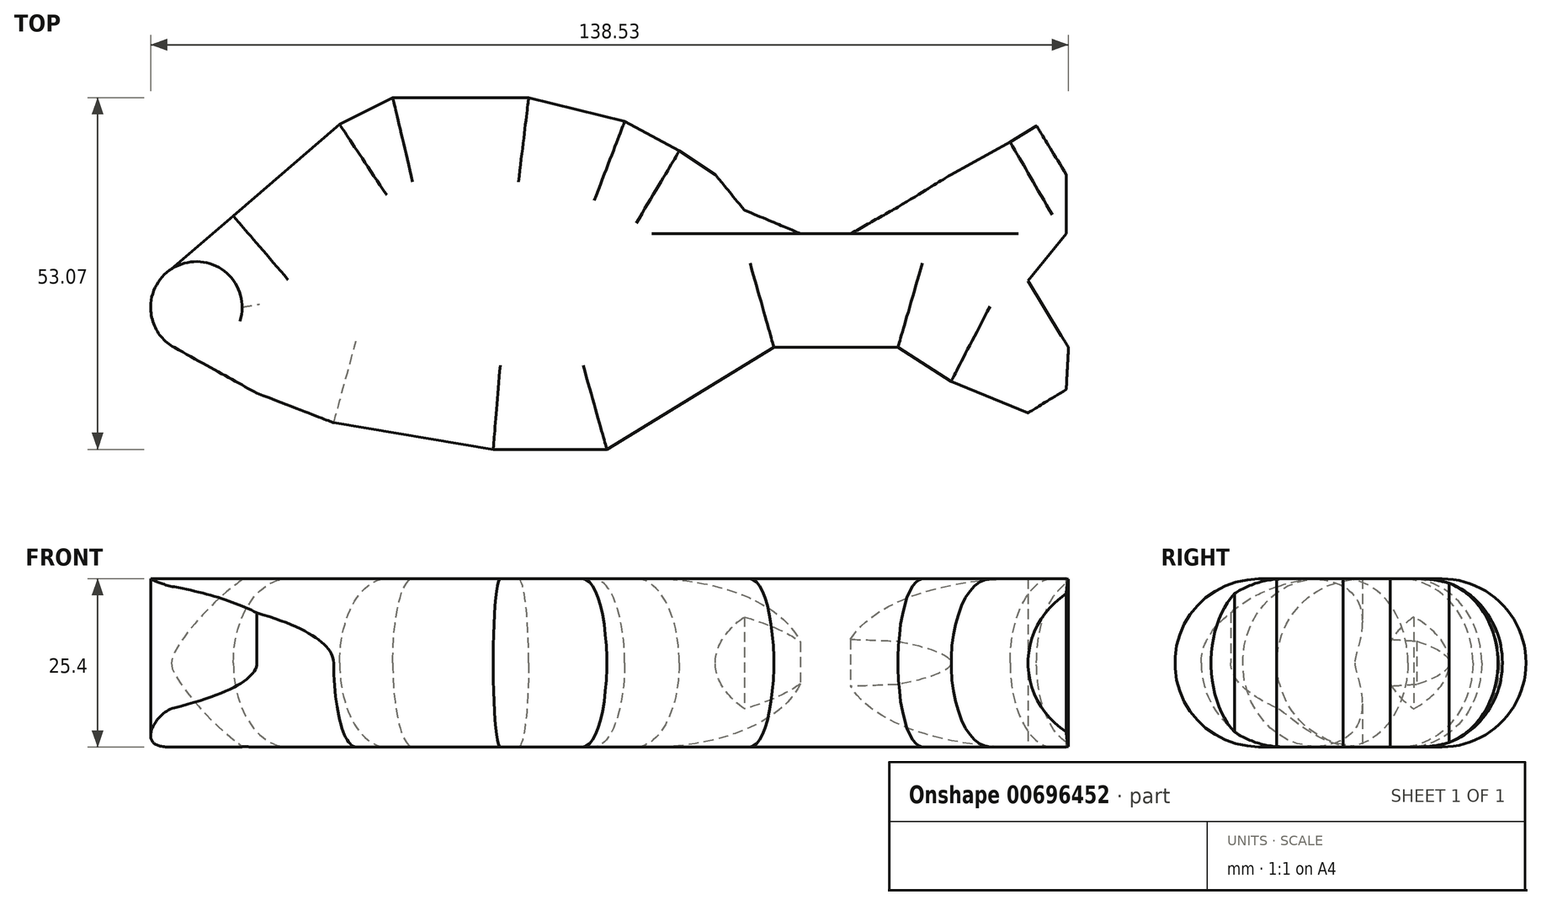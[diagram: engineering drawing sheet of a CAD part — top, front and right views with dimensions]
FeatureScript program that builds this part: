
annotation { "Feature Type Name" : "Feature", "Feature Type Description" : "" }
export const myFeature = defineFeature(function(context is Context, id is Id, definition is map)
    precondition{}
    {
        {
            var Q0;
            Q0=qCreatedBy(makeId("Top.planeOp"),FACE);
            var sketch = newSketch(context, id + "F0", { "sketchPlane" : qUnion([Q0])});
            skLineSegment(sketch, "E0", {"start": v(-59.07, 19.84) * mm, "end": v(-43.02, 33.66) * mm});
            skLineSegment(sketch, "E1", {"start": v(-43.02, 33.66) * mm, "end": v(-35, 37.67) * mm});
            skLineSegment(sketch, "E2", {"start": v(-35, 37.67) * mm, "end": v(-30.98, 37.67) * mm});
            skLineSegment(sketch, "E3", {"start": v(-30.98, 37.67) * mm, "end": v(-14.49, 37.67) * mm});
            skLineSegment(sketch, "E4", {"start": v(-14.49, 37.67) * mm, "end": v(0, 34.1) * mm});
            skLineSegment(sketch, "E5", {"start": v(0, 34.1) * mm, "end": v(8.25, 29.65) * mm});
            skLineSegment(sketch, "E6", {"start": v(8.25, 29.65) * mm, "end": v(13.68, 26.08) * mm});
            skLineSegment(sketch, "E7", {"start": v(13.68, 26.08) * mm, "end": v(18.06, 20.73) * mm});
            skLineSegment(sketch, "E8", {"start": v(18.06, 20.73) * mm, "end": v(26.53, 17.16) * mm});
            skLineSegment(sketch, "E9", {"start": v(26.53, 17.16) * mm, "end": v(34.1, 17.16) * mm});
            skLineSegment(sketch, "E10", {"start": v(34.1, 17.16) * mm, "end": v(41.24, 21.18) * mm});
            skLineSegment(sketch, "E11", {"start": v(41.24, 21.18) * mm, "end": v(49.26, 26.08) * mm});
            skLineSegment(sketch, "E12", {"start": v(49.26, 26.08) * mm, "end": v(58.18, 30.98) * mm});
            skLineSegment(sketch, "E13", {"start": v(58.18, 30.98) * mm, "end": v(62.17, 33.42) * mm});
            skLineSegment(sketch, "E14", {"start": v(62.17, 33.42) * mm, "end": v(66.65, 26.08) * mm});
            skLineSegment(sketch, "E15", {"start": v(66.65, 26.08) * mm, "end": v(66.65, 17.16) * mm});
            skLineSegment(sketch, "E16", {"start": v(66.65, 17.16) * mm, "end": v(60.85, 10.03) * mm});
            skLineSegment(sketch, "E17", {"start": v(60.85, 10.03) * mm, "end": v(66.98, 0) * mm});
            skLineSegment(sketch, "E18", {"start": v(66.98, 0) * mm, "end": v(66.65, -6.35) * mm});
            skLineSegment(sketch, "E19", {"start": v(66.65, -6.35) * mm, "end": v(60.85, -9.9) * mm});
            skLineSegment(sketch, "E20", {"start": v(60.85, -9.9) * mm, "end": v(49.26, -5.13) * mm});
            skLineSegment(sketch, "E21", {"start": v(49.26, -5.13) * mm, "end": v(41.24, 0) * mm});
            skLineSegment(sketch, "E22", {"start": v(41.24, 0) * mm, "end": v(32.32, 0) * mm});
            skLineSegment(sketch, "E23", {"start": v(32.32, 0) * mm, "end": v(22.51, 0) * mm});
            skLineSegment(sketch, "E24", {"start": v(22.51, 0) * mm, "end": v(17.7, -2.94) * mm});
            skLineSegment(sketch, "E25", {"start": v(17.7, -2.94) * mm, "end": v(5.25, -10.55) * mm});
            skLineSegment(sketch, "E26", {"start": v(5.25, -10.55) * mm, "end": v(-2.69, -15.4) * mm});
            skLineSegment(sketch, "E27", {"start": v(-2.69, -15.4) * mm, "end": v(-19.84, -15.4) * mm});
            skLineSegment(sketch, "E28", {"start": v(-19.84, -15.4) * mm, "end": v(-43.91, -11.37) * mm});
            skLineSegment(sketch, "E29", {"start": v(-43.91, -11.37) * mm, "end": v(-55.5, -6.91) * mm});
            skLineSegment(sketch, "E30", {"start": v(-59.07, 19.84) * mm, "end": v(-68.43, 11.81) * mm});
            skLineSegment(sketch, "E31", {"start": v(-55.5, -6.91) * mm, "end": v(-67.99, 0) * mm});
            skArc(sketch, "E32", {"start": v(-68.43, 11.81) * mm, "mid": v(-71.54, 5.78) * mm, "end": v(-67.99, 0) * mm});
            skSolve(sketch);
        }
        {
            var Q0;
            Q0 = qSketchRegion(id + "F0", true);
            extrude(context, id + "F1", {"entities" : qUnion([Q0]), "depth" : 25.4 * mm, "offsetDistance" : 25.4 * mm});
        }
        {
            var Q0;
            Q0=makeQuery(id+"F1.opExtrude","CAP_EDGE",EDGE,{"disambiguationData":[OSD([sQuery(id+"F0.wireOp",EDGE,"E0")])],"isStart":false});
            var Q1;
            Q1=makeQuery(id+"F1.opExtrude","CAP_EDGE",EDGE,{"disambiguationData":[OSD([sQuery(id+"F0.wireOp",EDGE,"E1")])],"isStart":false});
            var Q2;
            Q2=makeQuery(id+"F1.opExtrude","CAP_EDGE",EDGE,{"disambiguationData":[OSD([sQuery(id+"F0.wireOp",EDGE,"E2"),sQuery(id+"F0.wireOp",EDGE,"E3")])],"isStart":false});
            var Q3;
            Q3=makeQuery(id+"F1.opExtrude","CAP_EDGE",EDGE,{"disambiguationData":[OSD([sQuery(id+"F0.wireOp",EDGE,"E4")])],"isStart":false});
            var Q4;
            Q4=makeQuery(id+"F1.opExtrude","CAP_EDGE",EDGE,{"disambiguationData":[OSD([sQuery(id+"F0.wireOp",EDGE,"E5")])],"isStart":false});
            var Q5;
            Q5=makeQuery(id+"F1.opExtrude","CAP_EDGE",EDGE,{"disambiguationData":[OSD([sQuery(id+"F0.wireOp",EDGE,"E6")])],"isStart":false});
            fillet(context, id + "F2", {"entities" : qUnion([Q0, Q1, Q2, Q3, Q4, Q5]), "radius" : 12.7 * mm, "tangentPropagation" : true, "allowEdgeOverflow" : false});
        }
        {
            var Q0;
            Q0=makeQuery(id+"F1.opExtrude","CAP_EDGE",EDGE,{"disambiguationData":[OSD([sQuery(id+"F0.wireOp",EDGE,"E2"),sQuery(id+"F0.wireOp",EDGE,"E3")])],"isStart":true});
            var Q1;
            Q1=makeQuery(id+"F1.opExtrude","CAP_EDGE",EDGE,{"disambiguationData":[OSD([sQuery(id+"F0.wireOp",EDGE,"E4")])],"isStart":true});
            var Q2;
            Q2=makeQuery(id+"F1.opExtrude","CAP_EDGE",EDGE,{"disambiguationData":[OSD([sQuery(id+"F0.wireOp",EDGE,"E5")])],"isStart":true});
            var Q3;
            Q3=makeQuery(id+"F1.opExtrude","CAP_EDGE",EDGE,{"disambiguationData":[OSD([sQuery(id+"F0.wireOp",EDGE,"E0")])],"isStart":true});
            var Q4;
            Q4=makeQuery(id+"F1.opExtrude","CAP_EDGE",EDGE,{"disambiguationData":[OSD([sQuery(id+"F0.wireOp",EDGE,"E1")])],"isStart":true});
            var Q5;
            Q5=makeQuery(id+"F1.opExtrude","CAP_EDGE",EDGE,{"disambiguationData":[OSD([sQuery(id+"F0.wireOp",EDGE,"E6")])],"isStart":true});
            var Q6;
            Q6=makeQuery(id+"F1.opExtrude","CAP_EDGE",EDGE,{"disambiguationData":[OSD([sQuery(id+"F0.wireOp",EDGE,"E28")])],"isStart":true});
            var Q7;
            Q7=makeQuery(id+"F1.opExtrude","CAP_EDGE",EDGE,{"disambiguationData":[OSD([sQuery(id+"F0.wireOp",EDGE,"E29")])],"isStart":true});
            var Q8;
            Q8=makeQuery(id+"F1.opExtrude","CAP_EDGE",EDGE,{"disambiguationData":[OSD([sQuery(id+"F0.wireOp",EDGE,"E27")])],"isStart":true});
            var Q9;
            Q9=makeQuery(id+"F1.opExtrude","CAP_EDGE",EDGE,{"disambiguationData":[OSD([sQuery(id+"F0.wireOp",EDGE,"E24"),sQuery(id+"F0.wireOp",EDGE,"E25"),sQuery(id+"F0.wireOp",EDGE,"E26")])],"isStart":true});
            var Q10;
            Q10=makeQuery(id+"F1.opExtrude","CAP_EDGE",EDGE,{"disambiguationData":[OSD([sQuery(id+"F0.wireOp",EDGE,"E22"),sQuery(id+"F0.wireOp",EDGE,"E23")])],"isStart":true});
            var Q11;
            Q11=makeQuery(id+"F1.opExtrude","CAP_EDGE",EDGE,{"disambiguationData":[OSD([sQuery(id+"F0.wireOp",EDGE,"E21")])],"isStart":true});
            var Q12;
            Q12=makeQuery(id+"F1.opExtrude","CAP_EDGE",EDGE,{"disambiguationData":[OSD([sQuery(id+"F0.wireOp",EDGE,"E20")])],"isStart":true});
            var Q13;
            Q13=makeQuery(id+"F1.opExtrude","CAP_EDGE",EDGE,{"disambiguationData":[OSD([sQuery(id+"F0.wireOp",EDGE,"E12")])],"isStart":true});
            var Q14;
            Q14=makeQuery(id+"F1.opExtrude","CAP_EDGE",EDGE,{"disambiguationData":[OSD([sQuery(id+"F0.wireOp",EDGE,"E20")])],"isStart":false});
            var Q15;
            Q15=makeQuery(id+"F1.opExtrude","CAP_EDGE",EDGE,{"disambiguationData":[OSD([sQuery(id+"F0.wireOp",EDGE,"E21")])],"isStart":false});
            var Q16;
            Q16=makeQuery(id+"F1.opExtrude","CAP_EDGE",EDGE,{"disambiguationData":[OSD([sQuery(id+"F0.wireOp",EDGE,"E22"),sQuery(id+"F0.wireOp",EDGE,"E23")])],"isStart":false});
            var Q17;
            Q17=makeQuery(id+"F1.opExtrude","CAP_EDGE",EDGE,{"disambiguationData":[OSD([sQuery(id+"F0.wireOp",EDGE,"E24"),sQuery(id+"F0.wireOp",EDGE,"E25"),sQuery(id+"F0.wireOp",EDGE,"E26")])],"isStart":false});
            var Q18;
            Q18=makeQuery(id+"F1.opExtrude","CAP_EDGE",EDGE,{"disambiguationData":[OSD([sQuery(id+"F0.wireOp",EDGE,"E28")])],"isStart":false});
            var Q19;
            Q19=makeQuery(id+"F1.opExtrude","CAP_EDGE",EDGE,{"disambiguationData":[OSD([sQuery(id+"F0.wireOp",EDGE,"E27")])],"isStart":false});
            fillet(context, id + "F3", {"entities" : qUnion([Q0, Q1, Q2, Q3, Q4, Q5, Q6, Q7, Q8, Q9, Q10, Q11, Q12, Q13, Q14, Q15, Q16, Q17, Q18, Q19]), "radius" : 12.7 * mm, "tangentPropagation" : true, "allowEdgeOverflow" : false});
        }
        {
            var Q0;
            Q0=makeQuery(id+"F1.opExtrude","CAP_EDGE",EDGE,{"disambiguationData":[OSD([sQuery(id+"F0.wireOp",EDGE,"E28")])],"isStart":false});
            var Q1;
            Q1=makeQuery(id+"F1.opExtrude","CAP_EDGE",EDGE,{"disambiguationData":[OSD([sQuery(id+"F0.wireOp",EDGE,"E29")])],"isStart":false});
            var Q2;
            Q2=makeQuery(id+"F1.opExtrude","CAP_EDGE",EDGE,{"disambiguationData":[OSD([sQuery(id+"F0.wireOp",EDGE,"E27")])],"isStart":false});
            var Q3;
            Q3=makeQuery(id+"F1.opExtrude","CAP_EDGE",EDGE,{"disambiguationData":[OSD([sQuery(id+"F0.wireOp",EDGE,"E24"),sQuery(id+"F0.wireOp",EDGE,"E25"),sQuery(id+"F0.wireOp",EDGE,"E26")])],"isStart":false});
            var Q4;
            Q4=makeQuery(id+"F1.opExtrude","CAP_EDGE",EDGE,{"disambiguationData":[OSD([sQuery(id+"F0.wireOp",EDGE,"E22"),sQuery(id+"F0.wireOp",EDGE,"E23")])],"isStart":false});
            var Q5;
            Q5=makeQuery(id+"F1.opExtrude","CAP_EDGE",EDGE,{"disambiguationData":[OSD([sQuery(id+"F0.wireOp",EDGE,"E21")])],"isStart":false});
            var Q6;
            Q6=makeQuery(id+"F1.opExtrude","CAP_EDGE",EDGE,{"disambiguationData":[OSD([sQuery(id+"F0.wireOp",EDGE,"E14")])],"isStart":false});
            var Q7;
            Q7=makeQuery(id+"F1.opExtrude","CAP_EDGE",EDGE,{"disambiguationData":[OSD([sQuery(id+"F0.wireOp",EDGE,"E12")])],"isStart":false});
            fillet(context, id + "F4", {"entities" : qUnion([Q0, Q1, Q2, Q3, Q4, Q5, Q6, Q7]), "radius" : 12.7 * mm, "tangentPropagation" : true, "allowEdgeOverflow" : false});
        }
    });
